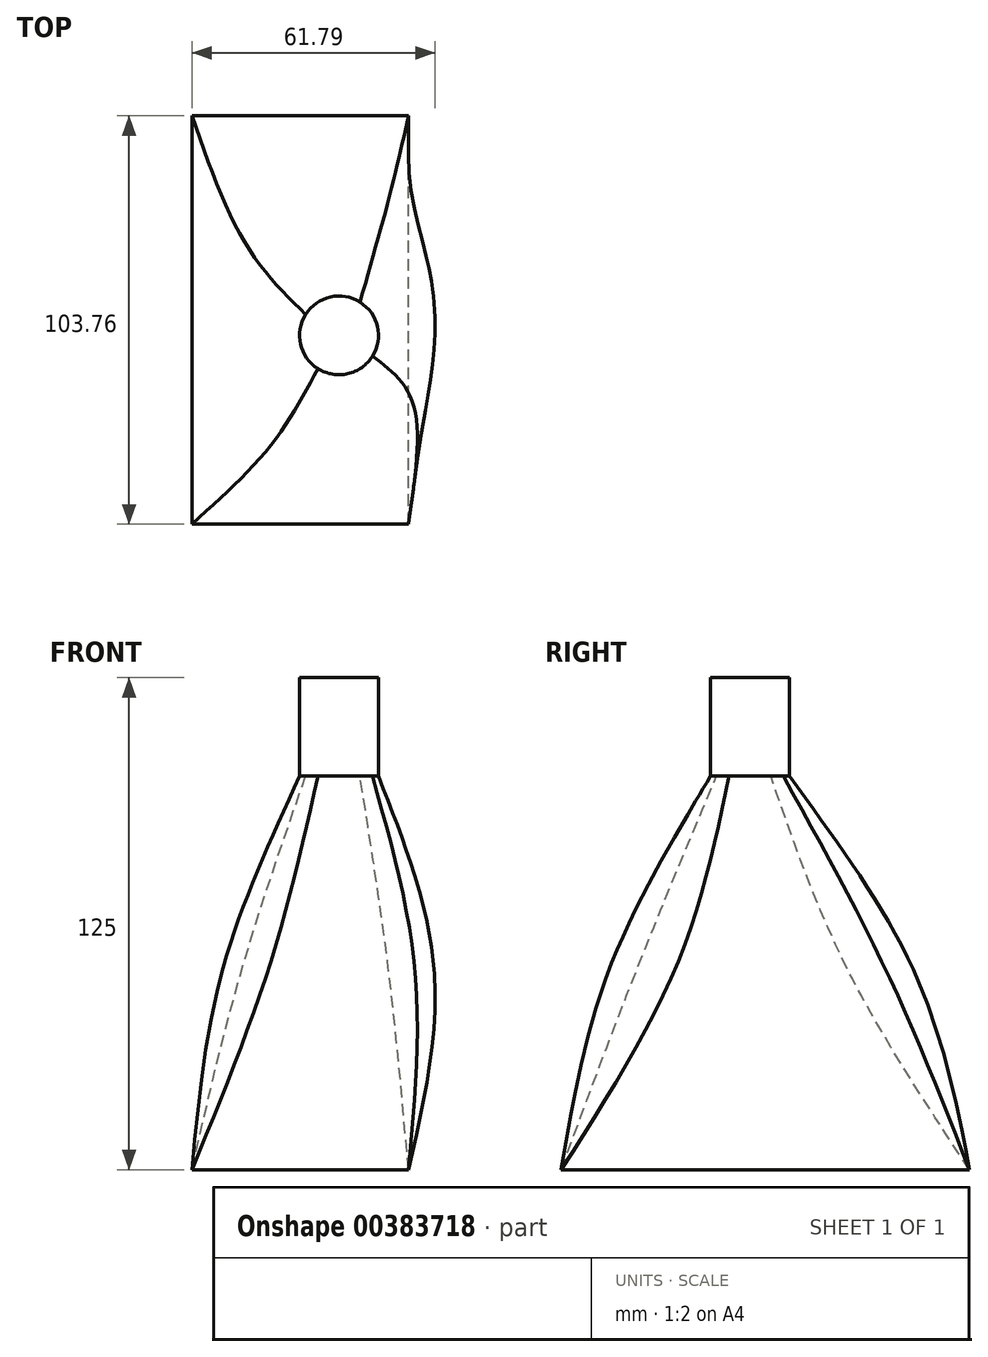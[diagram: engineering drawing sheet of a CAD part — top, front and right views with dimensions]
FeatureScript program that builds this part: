
annotation { "Feature Type Name" : "Feature", "Feature Type Description" : "" }
export const myFeature = defineFeature(function(context is Context, id is Id, definition is map)
    precondition{}
    {
        {
            var Q0;
            Q0=qCreatedBy(makeId("Top.planeOp"),FACE);
            var sketch = newSketch(context, id + "F0", { "sketchPlane" : qUnion([Q0])});
            skLineSegment(sketch, "E0.bottom", {"start": v(-27.26, -51.74) * mm, "end": v(27.74, -51.74) * mm});
            skLineSegment(sketch, "E0.top", {"start": v(-27.26, 52.02) * mm, "end": v(27.74, 52.02) * mm});
            skLineSegment(sketch, "E0.left", {"start": v(-27.26, -51.74) * mm, "end": v(-27.26, 52.02) * mm});
            skLineSegment(sketch, "E0.right", {"start": v(27.74, -51.74) * mm, "end": v(27.74, 52.02) * mm});
            skSolve(sketch);
        }
        {
            var Q0;
            Q0=qCreatedBy(makeId("Top.planeOp"),FACE);
            cPlane(context, id + "F1", {"entities" : qUnion([Q0]), "cplaneType" : CPlaneType.OFFSET, "offset" : 50 * mm, "width" : 152.4 * mm, "height" : 152.4 * mm});
        }
        {
            var Q0;
            Q0=qCreatedBy(id+"F1.planeOp",FACE);
            var sketch = newSketch(context, id + "F2", { "sketchPlane" : qUnion([Q0])});
            skEllipse(sketch, "E1", {"center": v(7.32, -0.86) * mm, "majorRadius": 39 * mm, "minorRadius": 27 * mm, "majorAxis": v(0, -1)});
            skSolve(sketch);
        }
        {
            var Q0;
            Q0=qCreatedBy(id+"F1.planeOp",FACE);
            cPlane(context, id + "F3", {"entities" : qUnion([Q0]), "cplaneType" : CPlaneType.OFFSET, "offset" : 50 * mm, "width" : 150 * mm, "height" : 150 * mm});
        }
        {
            var Q0;
            Q0=qCreatedBy(id+"F3.planeOp",FACE);
            var sketch = newSketch(context, id + "F4", { "sketchPlane" : qUnion([Q0])});
            skCircle(sketch, "E2", {"center": v(10.11, -3.77) * mm, "radius": 10 * mm});
            skPoint(sketch, "E2.first.point", {"position": v(4.41, -11.99) * mm});
            skPoint(sketch, "E2.second.point", {"position": v(20.05, -4.83) * mm});
            skPoint(sketch, "E2.third.point", {"position": v(4.3, 4.36) * mm});
            skSolve(sketch);
        }
        {
            var Q0;
            Q0 = qSketchRegion(id + "F0", true);
            var Q1;
            Q1 = qSketchRegion(id + "F2", true);
            var Q2;
            Q2 = qSketchRegion(id + "F4", true);
            loft(context, id + "F5", {"sheetProfilesArray" : [{ "sheetProfileEntities" : qUnion([Q0]) }, { "sheetProfileEntities" : qUnion([Q1]) }, { "sheetProfileEntities" : qUnion([Q2]) }]});
        }
        {
            var Q0;
            Q0=makeQuery(id+"F5.opLoft","CAP_FACE",FACE,{"disambiguationData":[OSD([makeQuery(id+"F4.imprint","IMPRINT",FACE,{"disambiguationData":[TD([[makeQuery(id+"F4.imprint","IMPRINT",EDGE,{"derivedFrom":sQuery(id+"F4.wireOp",EDGE,"E2")}),1.0]])]})])],"isStart":true});
            extrude(context, id + "F6", {"entities" : qUnion([Q0]), "depth" : 25 * mm});
        }
    });
